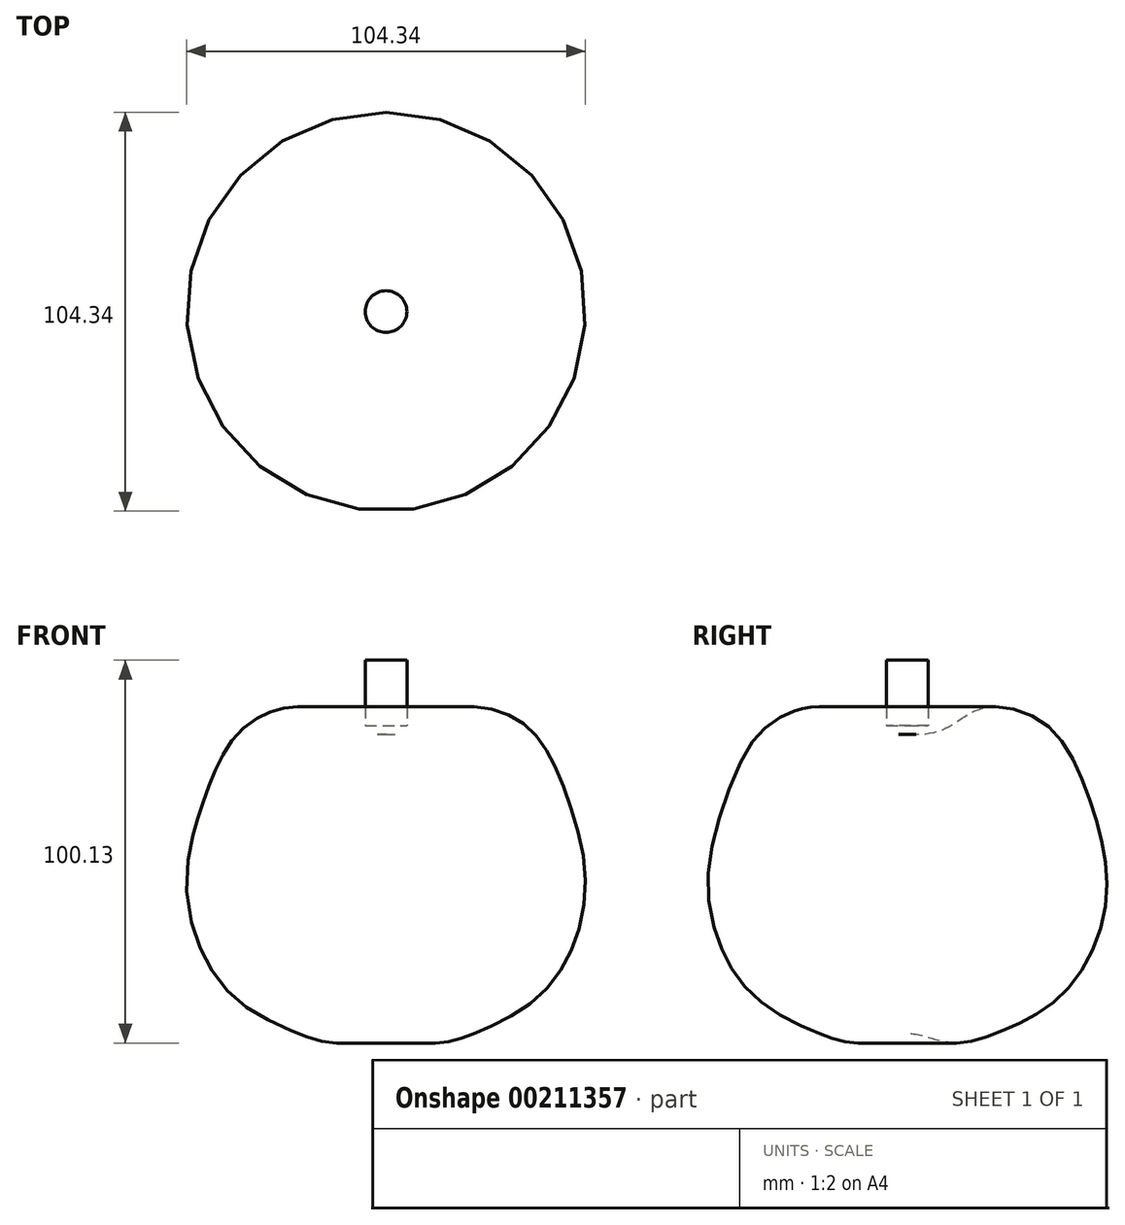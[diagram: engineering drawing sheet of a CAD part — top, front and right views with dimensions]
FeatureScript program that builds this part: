
annotation { "Feature Type Name" : "Feature", "Feature Type Description" : "" }
export const myFeature = defineFeature(function(context is Context, id is Id, definition is map)
    precondition{}
    {
        {
            var Q0;
            Q0=qCreatedBy(makeId("Right.planeOp"),FACE);
            var sketch = newSketch(context, id + "F0", { "sketchPlane" : qUnion([Q0])});
            skFitSpline(sketch, "E0", {"points": [v(-13.52, 42.88) * mm, v(-6.05, 38.04) * mm, v(8.68, 37.63) * mm, v(19.17, 43.28) * mm, v(36.12, 39.25) * mm, v(47.62, 19.47) * mm, v(52.06, -5.35) * mm, v(41.97, -29.97) * mm, v(24.42, -41.06) * mm, v(11.7, -44.1) * mm, v(0, -41.67) * mm, v(-10.09, -44.1) * mm], "startDerivative": vector(93.44, -81.37) * mm, "endDerivative": vector(-135.68, -53.75) * mm});
            skLineSegment(sketch, "E1", {"start": v(0, 36.75) * mm, "end": v(0, -41.67) * mm});
            skLineSegment(sketch, "E2", {"start": v(0, 51.76) * mm, "end": v(4.04, 51.76) * mm});
            skLineSegment(sketch, "E3", {"start": v(4.04, 51.76) * mm, "end": v(4.04, 36.75) * mm});
            skSolve(sketch);
        }
        {
            var Q0;
            {var subQ0=sQuery(id+"F0.wireOp",EDGE,"E1");Q0=makeQuery(id+"F0.imprint","IMPRINT",FACE,{"disambiguationData":[TD([[makeQuery(id+"F0.imprint","IMPRINT",EDGE,{"derivedFrom":subQ0}),1.0]])]});}
            var Q1;
            Q1=sQuery(id+"F0.wireOp",EDGE,"E1");
            revolve(context, id + "F1", {"entities" : qUnion([Q0]), "axis" : qUnion([Q1]), "revolveType" : RevolveType.FULL});
        }
        {
            var Q0;
            Q0=qCreatedBy(makeId("Right.planeOp"),FACE);
            var sketch = newSketch(context, id + "F2", { "sketchPlane" : qUnion([Q0])});
            skLineSegment(sketch, "E4", {"start": v(0, 56) * mm, "end": v(5.45, 56) * mm});
            skLineSegment(sketch, "E5", {"start": v(5.45, 56) * mm, "end": v(5.45, 38.84) * mm});
            skLineSegment(sketch, "E6", {"start": v(5.45, 38.84) * mm, "end": v(0, 38.84) * mm});
            skLineSegment(sketch, "E7", {"start": v(0, 38.84) * mm, "end": v(0, 56) * mm});
            skSolve(sketch);
        }
        {
            var Q0;
            Q0=makeQuery(id+"F2.imprint","IMPRINT",FACE,{"disambiguationData":[TD([[makeQuery(id+"F2.imprint","IMPRINT",EDGE,{"derivedFrom":sQuery(id+"F2.wireOp",EDGE,"E4")}),-1.0]])]});
            var Q1;
            Q1=sQuery(id+"F2.wireOp",EDGE,"E7");
            revolve(context, id + "F3", {"entities" : qUnion([Q0]), "axis" : qUnion([Q1]), "revolveType" : RevolveType.FULL});
        }
    });
